# Revit family: Displays_Tensioner_J-End
name_source: partatom
category: Generic Models
units: mm (PartAtom-declared; Revit-internal decimal feet)

## family parameters
Always vertical = Yes
Can host rebar = No
Classification Number = 23.40.90.11
Cut with Voids When Loaded = No
Maintain Annotation Orientation = No
Part Type = Normal
Room Calculation Point = No
Round Connector Dimension = Use Diameter
Shared = No
Work Plane-Based = Yes

## types (1)
- As Specified
    Cable Material = Stainless Steel
    Default Elevation = 4' - 0"
    Description = AS Hanging J End Tensioner
    Hook = Stainless Steel
    Keynote = 10 14 00
    Manufacturer = AS Hanging
    Manufacturer Website = https://www.ashanging.com
    Model = J End Tensioner
    Overall Height = 0' - 5 23/32"
    Product Data = http://www.arcat.com
    Revision = R1_2017
    Sales Information = https://www.ashanging.com
    Specification = http://www.arcat.com
    Thickness = 0' - 0 5/32"
    URL = https://www.ashanging.com

## geometry (parser evidence)
native form markers: Sweep x2
no freeform markers — native parametric forms only
